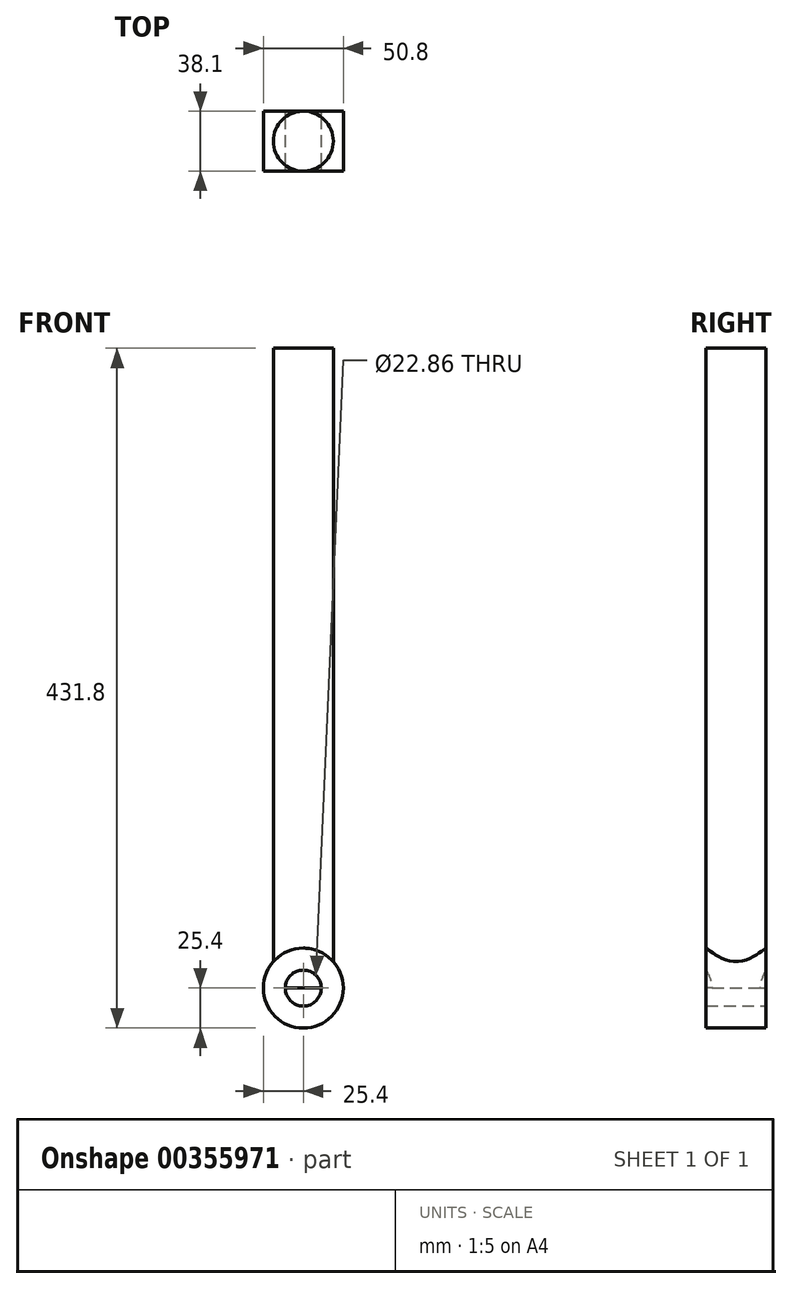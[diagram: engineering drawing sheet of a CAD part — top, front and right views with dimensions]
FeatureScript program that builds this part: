
annotation { "Feature Type Name" : "Feature", "Feature Type Description" : "" }
export const myFeature = defineFeature(function(context is Context, id is Id, definition is map)
    precondition{}
    {
        {
            var Q0;
            Q0=qCreatedBy(makeId("Top.planeOp"),FACE);
            var sketch = newSketch(context, id + "F0", { "sketchPlane" : qUnion([Q0])});
            skCircle(sketch, "E0", {"center": v(0, 0) * mm, "radius": 19.05 * mm});
            skSolve(sketch);
        }
        {
            var Q0;
            Q0=qCreatedBy(makeId("Front.planeOp"),FACE);
            var sketch = newSketch(context, id + "F1", { "sketchPlane" : qUnion([Q0])});
            skCircle(sketch, "E1", {"center": v(0, 0) * mm, "radius": 11.43 * mm});
            skCircle(sketch, "E2", {"center": v(0, 0) * mm, "radius": 25.4 * mm});
            skSolve(sketch);
        }
        {
            var Q0;
            Q0=makeQuery(id+"F1.imprint","IMPRINT",FACE,{"disambiguationData":[TD([[makeQuery(id+"F1.imprint","IMPRINT",EDGE,{"derivedFrom":sQuery(id+"F1.wireOp",EDGE,"E1")}),-1.0]])]});
            extrude(context, id + "F2", {"entities" : qUnion([Q0]), "endBound" : BoundingType.SYMMETRIC, "depth" : 38.1 * mm});
        }
        {
            var Q0;
            Q0=makeQuery(id+"F0.imprint","IMPRINT",FACE,{"disambiguationData":[TD([[makeQuery(id+"F0.imprint","IMPRINT",EDGE,{"derivedFrom":sQuery(id+"F0.wireOp",EDGE,"E0")}),1.0]])]});
            extrude(context, id + "F3", {"entities" : qUnion([Q0]), "operationType" : NewBodyOperationType.ADD, "depth" : 254 * mm});
        }
        {
            var Q0;
            Q0=makeQuery(id+"F3.opExtrude","CAP_FACE",FACE,{"disambiguationData":[OSD([sQuery(id+"F0.wireOp",EDGE,"E0")])],"isStart":false});
            var sketch = newSketch(context, id + "F4", { "sketchPlane" : qUnion([Q0])});
            skCircle(sketch, "E3", {"center": v(0, 0) * mm, "radius": 38.1 * mm});
            skSolve(sketch);
        }
        {
            var Q0;
            Q0=makeQuery(id+"F4.imprint","IMPRINT",FACE,{"disambiguationData":[TD([[makeQuery(id+"F4.imprint","IMPRINT",EDGE,{"derivedFrom":sQuery(id+"F4.wireOp",EDGE,"E3")}),1.0]])]});
            extrude(context, id + "F5", {"entities" : qUnion([Q0]), "depth" : 6.35 * mm});
        }
        {
            var Q0;
            Q0=makeQuery(id+"F3.opExtrude","CAP_FACE",FACE,{"disambiguationData":[OSD([sQuery(id+"F0.wireOp",EDGE,"E0")])],"isStart":false});
            extrude(context, id + "F6", {"entities" : qUnion([Q0]), "operationType" : NewBodyOperationType.ADD, "depth" : 152.4 * mm});
        }
        {
            var Q0;
            Q0=makeQuery(id+"F5.opExtrude","CAP_FACE",FACE,{"disambiguationData":[OSD([sQuery(id+"F0.wireOp",EDGE,"E0"),sQuery(id+"F4.wireOp",EDGE,"E3")])],"isStart":false});
            extrude(context, id + "F7", {"entities" : qUnion([Q0]), "operationType" : NewBodyOperationType.REMOVE, "oppositeDirection" : true, "depth" : 25.4 * mm});
        }
    });
